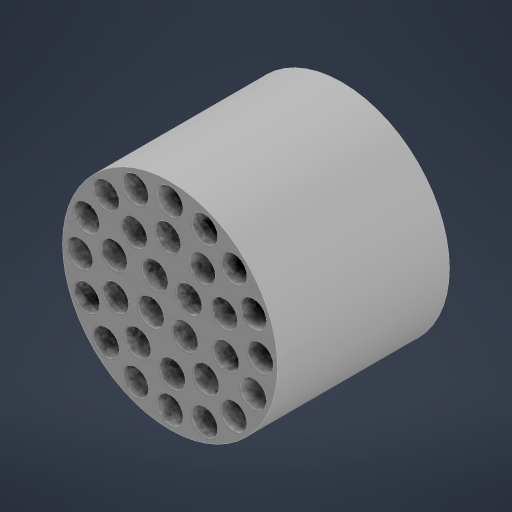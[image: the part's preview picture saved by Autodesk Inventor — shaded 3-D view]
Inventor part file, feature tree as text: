
AUTODESK INVENTOR PART (.ipt)
format: ipt  version: 2024 (Build 280153000, 153)  size: 338,944 bytes
history: native  units: mm
features: other x3, extrude x1, sketch x1
ambient origin geometry x8: Origin, YZ Plane, XZ Plane, XY Plane, X Axis, Y Axis, Z Axis, Center Point
bodies: Body1 (feature_tree)
feature tree (5):
  other  "Sólido1"
  extrude  "Extrusión1"  Depth=10.0mm TaperAngle=0.0deg
  other  "Edición directa1"
  sketch  "Boceto1"  dims[d6=160.0mm d8=360.0deg d21=20.0mm d22=0.0mm d32=100.0mm d34=360.0deg d37=40.0mm d39=360.0deg d41=68.248mm d42=10.0mm d43=10.0mm]
  other  "Escala1"
